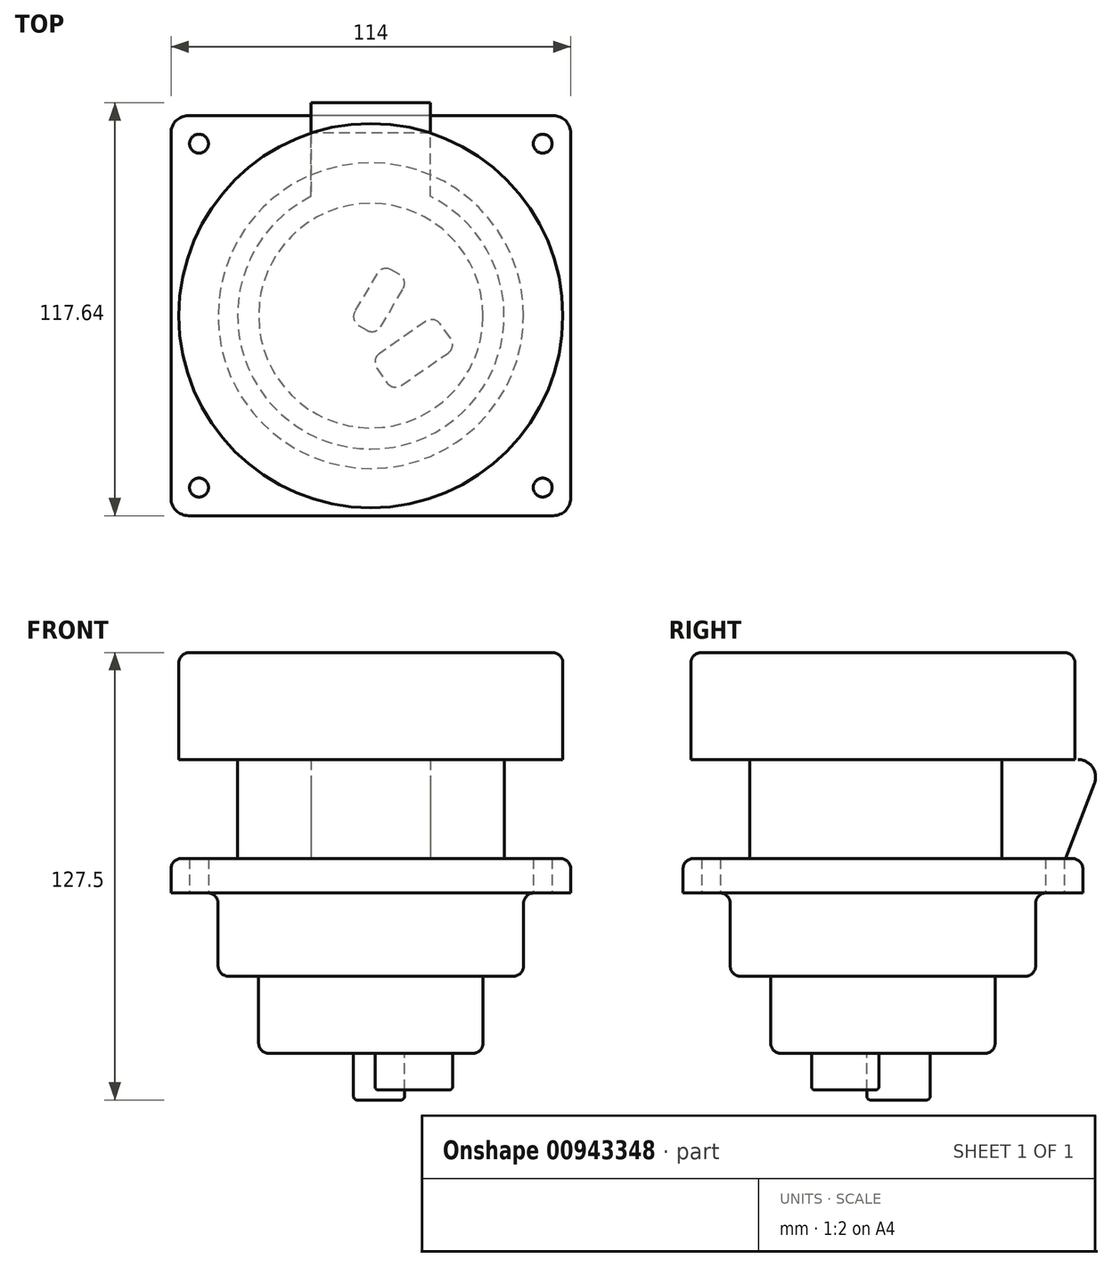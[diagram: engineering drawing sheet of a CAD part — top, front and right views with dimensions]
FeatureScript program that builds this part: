
annotation { "Feature Type Name" : "Feature", "Feature Type Description" : "" }
export const myFeature = defineFeature(function(context is Context, id is Id, definition is map)
    precondition{}
    {
        {
            var Q0;
            Q0=qCreatedBy(makeId("Top.planeOp"),FACE);
            var sketch = newSketch(context, id + "F0", { "sketchPlane" : qUnion([Q0])});
            skLineSegment(sketch, "E0.bottom", {"start": v(57, -57) * mm, "end": v(-57, -57) * mm});
            skLineSegment(sketch, "E0.top", {"start": v(57, 57) * mm, "end": v(-57, 57) * mm});
            skLineSegment(sketch, "E0.left", {"start": v(57, -57) * mm, "end": v(57, 57) * mm});
            skLineSegment(sketch, "E0.right", {"start": v(-57, -57) * mm, "end": v(-57, 57) * mm});
            skPoint(sketch, "E0.middle", {"position": v(0, 0) * mm});
            skCircle(sketch, "E1", {"center": v(-49, 49) * mm, "radius": 2.7 * mm});
            skCircle(sketch, "E2", {"center": v(49, 49) * mm, "radius": 2.7 * mm});
            skCircle(sketch, "E3.MirrorC", {"center": v(-49, -49) * mm, "radius": 2.7 * mm});
            skCircle(sketch, "E4.MirrorC", {"center": v(49, -49) * mm, "radius": 2.7 * mm});
            skCircle(sketch, "E5", {"center": v(0, 0) * mm, "radius": 38 * mm});
            skLineSegment(sketch, "E6.top", {"start": v(17, 61) * mm, "end": v(-17, 61) * mm});
            skLineSegment(sketch, "E6.left", {"start": v(17, 41) * mm, "end": v(17, 61) * mm});
            skLineSegment(sketch, "E6.right", {"start": v(-17, 41) * mm, "end": v(-17, 61) * mm});
            skPoint(sketch, "E6.middle", {"position": v(0, 51) * mm});
            skLineSegment(sketch, "E7", {"start": v(-17, 41) * mm, "end": v(-17, 33.99) * mm});
            skLineSegment(sketch, "E8", {"start": v(17, 41) * mm, "end": v(17, 33.99) * mm});
            skSolve(sketch);
        }
        {
            var Q0;
            Q0=makeQuery(id+"F0.imprint","IMPRINT",FACE,{"disambiguationData":[TD([[makeQuery(id+"F0.imprint","IMPRINT",EDGE,{"derivedFrom":sQuery(id+"F0.wireOp",EDGE,"E0.bottom")}),-1.0]])]});
            extrude(context, id + "F1", {"entities" : qUnion([Q0]), "depth" : 9.8 * mm, "offsetDistance" : 25 * mm});
        }
        {
            var Q0;
            {var subQ5=sQuery(id+"F0.wireOp",EDGE,"E6.top");Q0=makeQuery(id+"F0.imprint","IMPRINT",FACE,{"disambiguationData":[TD([[makeQuery(id+"F0.imprint","IMPRINT",EDGE,{"derivedFrom":subQ5}),1.0]])]});}
            var Q1;
            {var subQ6=sQuery(id+"F0.wireOp",EDGE,"E7");Q1=makeQuery(id+"F0.imprint","IMPRINT",FACE,{"disambiguationData":[TD([[makeQuery(id+"F0.imprint","IMPRINT",EDGE,{"derivedFrom":subQ6}),1.0]])]});}
            var Q2;
            {var subQ0=sQuery(id+"F0.wireOp",EDGE,"E5");var subQ1=makeQuery(id+"F0.imprint","INTERSECT",VERTEX,{"derivedFrom":[subQ0,sQuery(id+"F0.wireOp",EDGE,"E7")]});Q2=makeQuery(id+"F0.imprint","IMPRINT",FACE,{"disambiguationData":[TD([[makeQuery(id+"F0.imprint","IMPRINT",EDGE,{"disambiguationData":[TD([[subQ1,1.0]])],"derivedFrom":subQ0}),1.0]])]});}
            extrude(context, id + "F2", {"entities" : qUnion([Q0, Q1, Q2]), "operationType" : NewBodyOperationType.ADD, "depth" : 38 * mm, "offsetDistance" : 25 * mm});
        }
        {
            var Q0;
            Q0=makeQuery(id+"F2.opExtrude","CAP_FACE",FACE,{"disambiguationData":[OSD([sQuery(id+"F0.wireOp",EDGE,"E5"),sQuery(id+"F0.wireOp",EDGE,"E6.top"),sQuery(id+"F0.wireOp",EDGE,"E6.left"),sQuery(id+"F0.wireOp",EDGE,"E6.right"),sQuery(id+"F0.wireOp",EDGE,"E7"),sQuery(id+"F0.wireOp",EDGE,"E8")])],"isStart":false});
            var sketch = newSketch(context, id + "F3", { "sketchPlane" : qUnion([Q0])});
            skCircle(sketch, "E9", {"center": v(0, 0) * mm, "radius": 54.75 * mm});
            skSolve(sketch);
        }
        {
            var Q0;
            Q0 = qSketchRegion(id + "F3", true);
            extrude(context, id + "F4", {"entities" : qUnion([Q0]), "depth" : 30.5 * mm, "offsetDistance" : 25 * mm});
        }
        {
            var Q0;
            Q0=makeQuery(id+"F1.opExtrude","CAP_EDGE",EDGE,{"disambiguationData":[OSD([sQuery(id+"F0.wireOp",EDGE,"E0.right")])],"isStart":false});
            var Q1;
            Q1=makeQuery(id+"F4.opExtrude","CAP_EDGE",EDGE,{"disambiguationData":[OSD([sQuery(id+"F3.wireOp",EDGE,"E9")])],"isStart":false});
            var Q2;
            Q2=makeQuery(id+"F1.opExtrude","CAP_EDGE",EDGE,{"disambiguationData":[OSD([sQuery(id+"F0.wireOp",EDGE,"E0.bottom")])],"isStart":false});
            var Q3;
            Q3=makeQuery(id+"F1.opExtrude","CAP_EDGE",EDGE,{"disambiguationData":[OSD([sQuery(id+"F0.wireOp",EDGE,"E0.left")])],"isStart":false});
            var Q4;
            {var subQ0=sQuery(id+"F0.wireOp",EDGE,"E0.top");Q4=makeQuery(id+"F1.opExtrude","CAP_EDGE",EDGE,{"disambiguationData":[OSD([subQ0]),TDD([makeQuery(id+"F0.imprint","IMPRINT",EDGE,{"disambiguationData":[TD([[makeQuery(id+"F0.imprint","INTERSECT",VERTEX,{"derivedFrom":[subQ0,sQuery(id+"F0.wireOp",EDGE,"E0.left")]}),-1.0]])],"derivedFrom":subQ0})])],"isStart":false});}
            var Q5;
            {var subQ0=sQuery(id+"F0.wireOp",EDGE,"E0.top");Q5=makeQuery(id+"F1.opExtrude","CAP_EDGE",EDGE,{"disambiguationData":[OSD([subQ0]),TDD([makeQuery(id+"F0.imprint","IMPRINT",EDGE,{"disambiguationData":[TD([[makeQuery(id+"F0.imprint","INTERSECT",VERTEX,{"derivedFrom":[subQ0,sQuery(id+"F0.wireOp",EDGE,"E0.right")]}),1.0]])],"derivedFrom":subQ0})])],"isStart":false});}
            fillet(context, id + "F5", {"entities" : qUnion([Q0, Q1, Q2, Q3, Q4, Q5]), "radius" : 3 * mm, "tangentPropagation" : true, "allowEdgeOverflow" : false});
        }
        {
            var Q0;
            Q0=makeQuery(id+"F1.opExtrude","SWEPT_EDGE",EDGE,{"disambiguationData":[OSD([sQuery(id+"F0.wireOp",EDGE,"E0.top"),sQuery(id+"F0.wireOp",EDGE,"E0.left")])]});
            var Q1;
            Q1=makeQuery(id+"F1.opExtrude","SWEPT_EDGE",EDGE,{"disambiguationData":[OSD([sQuery(id+"F0.wireOp",EDGE,"E0.top"),sQuery(id+"F0.wireOp",EDGE,"E0.right")])]});
            var Q2;
            Q2=makeQuery(id+"F1.opExtrude","SWEPT_EDGE",EDGE,{"disambiguationData":[OSD([sQuery(id+"F0.wireOp",EDGE,"E0.bottom"),sQuery(id+"F0.wireOp",EDGE,"E0.left")])]});
            var Q3;
            Q3=makeQuery(id+"F1.opExtrude","SWEPT_EDGE",EDGE,{"disambiguationData":[OSD([sQuery(id+"F0.wireOp",EDGE,"E0.bottom"),sQuery(id+"F0.wireOp",EDGE,"E0.right")])]});
            var Q4;
            Q4=makeQuery(id+"F2.opExtrude","CAP_EDGE",EDGE,{"disambiguationData":[OSD([sQuery(id+"F0.wireOp",EDGE,"E6.top")])],"isStart":false});
            fillet(context, id + "F6", {"entities" : qUnion([Q0, Q1, Q2, Q3, Q4]), "radius" : 5 * mm, "tangentPropagation" : true, "allowEdgeOverflow" : false});
        }
        {
            var Q0;
            Q0=makeQuery(id+"F2.opExtrude","SWEPT_FACE",FACE,{"disambiguationData":[OSD([sQuery(id+"F0.wireOp",EDGE,"E6.right"),sQuery(id+"F0.wireOp",EDGE,"E7")])]});
            var sketch = newSketch(context, id + "F7", { "sketchPlane" : qUnion([Q0])});
            skLineSegment(sketch, "E10", {"start": v(-61, 33) * mm, "end": v(-52.05, 9.8) * mm});
            skSolve(sketch);
        }
        {
            var Q0;
            Q0 = qSketchRegion(id + "F7", true);
            var Q1;
            {var subQ4=sQuery(id+"F7.wireOp",EDGE,"E10");Q1=makeQuery(id+"F7.imprint","IMPRINT",FACE,{"disambiguationData":[TD([[makeQuery(id+"F7.imprint","IMPRINT",EDGE,{"derivedFrom":subQ4}),-1.0]])]});}
            extrude(context, id + "F8", {"entities" : qUnion([Q0, Q1]), "operationType" : NewBodyOperationType.REMOVE, "endBound" : BoundingType.THROUGH_ALL, "oppositeDirection" : true, "depth" : 25 * mm, "offsetDistance" : 25 * mm});
        }
        {
            var Q0;
            {var subQ0=sQuery(id+"F0.wireOp",EDGE,"E6.top");Q0=makeQuery(id+"F8.boolean.opBoolean","MERGE",EDGE,{"derivedFrom":[makeQuery(id+"F6.opFillet","BLEND_EDGE",EDGE,{"blendedFrom":[makeQuery(id+"F2.opExtrude","CAP_EDGE",EDGE,{"disambiguationData":[OSD([subQ0])],"isStart":false}),makeQuery(id+"F2.opExtrude","SWEPT_FACE",FACE,{"disambiguationData":[OSD([subQ0])]})],"blendedInto":[makeQuery(id+"F2.opExtrude","SWEPT_FACE",FACE,{"disambiguationData":[OSD([subQ0])]})]})],"fromTools":[makeQuery(id+"F8.opExtrude","SWEPT_EDGE",EDGE,{"disambiguationData":[OSD([subQ0,sQuery(id+"F0.wireOp",EDGE,"E6.right"),sQuery(id+"F0.wireOp",EDGE,"E7"),sQuery(id+"F7.wireOp",EDGE,"E10")])]})]});}
            fillet(context, id + "F9", {"entities" : qUnion([Q0]), "radius" : 5 * mm, "tangentPropagation" : true, "allowEdgeOverflow" : false});
        }
        {
            var Q0;
            Q0=makeQuery(id+"F0.imprint","IMPRINT",FACE,{"disambiguationData":[TD([[makeQuery(id+"F0.imprint","IMPRINT",EDGE,{"derivedFrom":sQuery(id+"F0.wireOp",EDGE,"E0.bottom")}),-1.0]])]});
            var sketch = newSketch(context, id + "F10", { "sketchPlane" : qUnion([Q0])});
            skCircle(sketch, "E11", {"center": v(0, 0) * mm, "radius": 43.55 * mm});
            skSolve(sketch);
        }
        {
            var Q0;
            Q0 = qSketchRegion(id + "F10", true);
            extrude(context, id + "F11", {"entities" : qUnion([Q0]), "operationType" : NewBodyOperationType.ADD, "oppositeDirection" : true, "depth" : 23.75 * mm, "offsetDistance" : 25 * mm});
        }
        {
            var Q0;
            Q0=makeQuery(id+"F11.opExtrude","CAP_FACE",FACE,{"disambiguationData":[OSD([sQuery(id+"F10.wireOp",EDGE,"E11")])],"isStart":false});
            var sketch = newSketch(context, id + "F12", { "sketchPlane" : qUnion([Q0])});
            skCircle(sketch, "E12", {"center": v(0, 0) * mm, "radius": 32 * mm});
            skSolve(sketch);
        }
        {
            var Q0;
            Q0 = qSketchRegion(id + "F12", true);
            extrude(context, id + "F13", {"entities" : qUnion([Q0]), "operationType" : NewBodyOperationType.ADD, "depth" : 22 * mm, "offsetDistance" : 25 * mm});
        }
        {
            var Q0;
            Q0=makeQuery(id+"F13.opExtrude","CAP_FACE",FACE,{"disambiguationData":[OSD([sQuery(id+"F12.wireOp",EDGE,"E12")])],"isStart":false});
            var sketch = newSketch(context, id + "F14", { "sketchPlane" : qUnion([Q0])});
            skLineSegment(sketch, "E13", {"start": v(18.03, 0) * mm, "end": v(0, 12.5) * mm});
            skLineSegment(sketch, "E14", {"start": v(0, 12.5) * mm, "end": v(6.28, 21.55) * mm});
            skLineSegment(sketch, "E15", {"start": v(6.28, 21.55) * mm, "end": v(24.57, 8.88) * mm});
            skLineSegment(sketch, "E16", {"start": v(24.57, 8.88) * mm, "end": v(18.03, 0) * mm});
            skLineSegment(sketch, "E17", {"start": v(3.2, -14.52) * mm, "end": v(-6.04, 1.32) * mm});
            skLineSegment(sketch, "E18", {"start": v(-6.04, 1.32) * mm, "end": v(1.4, 5.67) * mm});
            skLineSegment(sketch, "E19", {"start": v(1.4, 5.67) * mm, "end": v(10.72, -10.3) * mm});
            skLineSegment(sketch, "E20", {"start": v(10.72, -10.3) * mm, "end": v(3.2, -14.52) * mm});
            skSolve(sketch);
        }
        {
            var Q0;
            Q0=makeQuery(id+"F14.imprint","IMPRINT",FACE,{"disambiguationData":[TD([[makeQuery(id+"F14.imprint","IMPRINT",EDGE,{"derivedFrom":sQuery(id+"F14.wireOp",EDGE,"E17")}),-1.0]])]});
            extrude(context, id + "F15", {"entities" : qUnion([Q0]), "operationType" : NewBodyOperationType.ADD, "depth" : 13.25 * mm, "offsetDistance" : 25 * mm});
        }
        {
            var Q0;
            Q0=makeQuery(id+"F14.imprint","IMPRINT",FACE,{"disambiguationData":[TD([[makeQuery(id+"F14.imprint","IMPRINT",EDGE,{"derivedFrom":sQuery(id+"F14.wireOp",EDGE,"E13")}),-1.0]])]});
            extrude(context, id + "F16", {"entities" : qUnion([Q0]), "operationType" : NewBodyOperationType.ADD, "depth" : 10.4 * mm, "offsetDistance" : 25 * mm});
        }
        {
            var Q0;
            Q0=makeQuery(id+"F11.opExtrude","SWEPT_FACE",FACE,{"disambiguationData":[OSD([sQuery(id+"F10.wireOp",EDGE,"E11")])]});
            var Q1;
            Q1=makeQuery(id+"F13.opExtrude","CAP_EDGE",EDGE,{"disambiguationData":[OSD([sQuery(id+"F12.wireOp",EDGE,"E12")])],"isStart":false});
            var Q2;
            Q2=makeQuery(id+"F16.opExtrude","SWEPT_EDGE",EDGE,{"disambiguationData":[OSD([sQuery(id+"F14.wireOp",EDGE,"E15"),sQuery(id+"F14.wireOp",EDGE,"E16")])]});
            var Q3;
            Q3=makeQuery(id+"F16.opExtrude","SWEPT_EDGE",EDGE,{"disambiguationData":[OSD([sQuery(id+"F14.wireOp",EDGE,"E14"),sQuery(id+"F14.wireOp",EDGE,"E15")])]});
            var Q4;
            Q4=makeQuery(id+"F15.opExtrude","SWEPT_EDGE",EDGE,{"disambiguationData":[OSD([sQuery(id+"F14.wireOp",EDGE,"E18"),sQuery(id+"F14.wireOp",EDGE,"E19")])]});
            var Q5;
            Q5=makeQuery(id+"F15.opExtrude","SWEPT_EDGE",EDGE,{"disambiguationData":[OSD([sQuery(id+"F14.wireOp",EDGE,"E19"),sQuery(id+"F14.wireOp",EDGE,"E20")])]});
            var Q6;
            Q6=makeQuery(id+"F16.opExtrude","SWEPT_EDGE",EDGE,{"disambiguationData":[OSD([sQuery(id+"F14.wireOp",EDGE,"E13"),sQuery(id+"F14.wireOp",EDGE,"E14")])]});
            var Q7;
            Q7=makeQuery(id+"F16.opExtrude","SWEPT_EDGE",EDGE,{"disambiguationData":[OSD([sQuery(id+"F14.wireOp",EDGE,"E13"),sQuery(id+"F14.wireOp",EDGE,"E16")])]});
            var Q8;
            Q8=makeQuery(id+"F15.opExtrude","SWEPT_EDGE",EDGE,{"disambiguationData":[OSD([sQuery(id+"F14.wireOp",EDGE,"E17"),sQuery(id+"F14.wireOp",EDGE,"E18")])]});
            var Q9;
            Q9=makeQuery(id+"F15.opExtrude","SWEPT_EDGE",EDGE,{"disambiguationData":[OSD([sQuery(id+"F14.wireOp",EDGE,"E17"),sQuery(id+"F14.wireOp",EDGE,"E20")])]});
            fillet(context, id + "F17", {"entities" : qUnion([Q0, Q1, Q2, Q3, Q4, Q5, Q6, Q7, Q8, Q9]), "radius" : 3 * mm, "tangentPropagation" : true, "allowEdgeOverflow" : false});
        }
        {
            var Q0;
            Q0=makeQuery(id+"F16.opExtrude","CAP_FACE",FACE,{"disambiguationData":[OSD([sQuery(id+"F14.wireOp",EDGE,"E13"),sQuery(id+"F14.wireOp",EDGE,"E14"),sQuery(id+"F14.wireOp",EDGE,"E15"),sQuery(id+"F14.wireOp",EDGE,"E16")])],"isStart":false});
            var Q1;
            Q1=makeQuery(id+"F15.opExtrude","CAP_FACE",FACE,{"disambiguationData":[OSD([sQuery(id+"F14.wireOp",EDGE,"E17"),sQuery(id+"F14.wireOp",EDGE,"E18"),sQuery(id+"F14.wireOp",EDGE,"E19"),sQuery(id+"F14.wireOp",EDGE,"E20")])],"isStart":false});
            fillet(context, id + "F18", {"entities" : qUnion([Q0, Q1]), "radius" : 1 * mm, "tangentPropagation" : true, "allowEdgeOverflow" : false});
        }
    });
